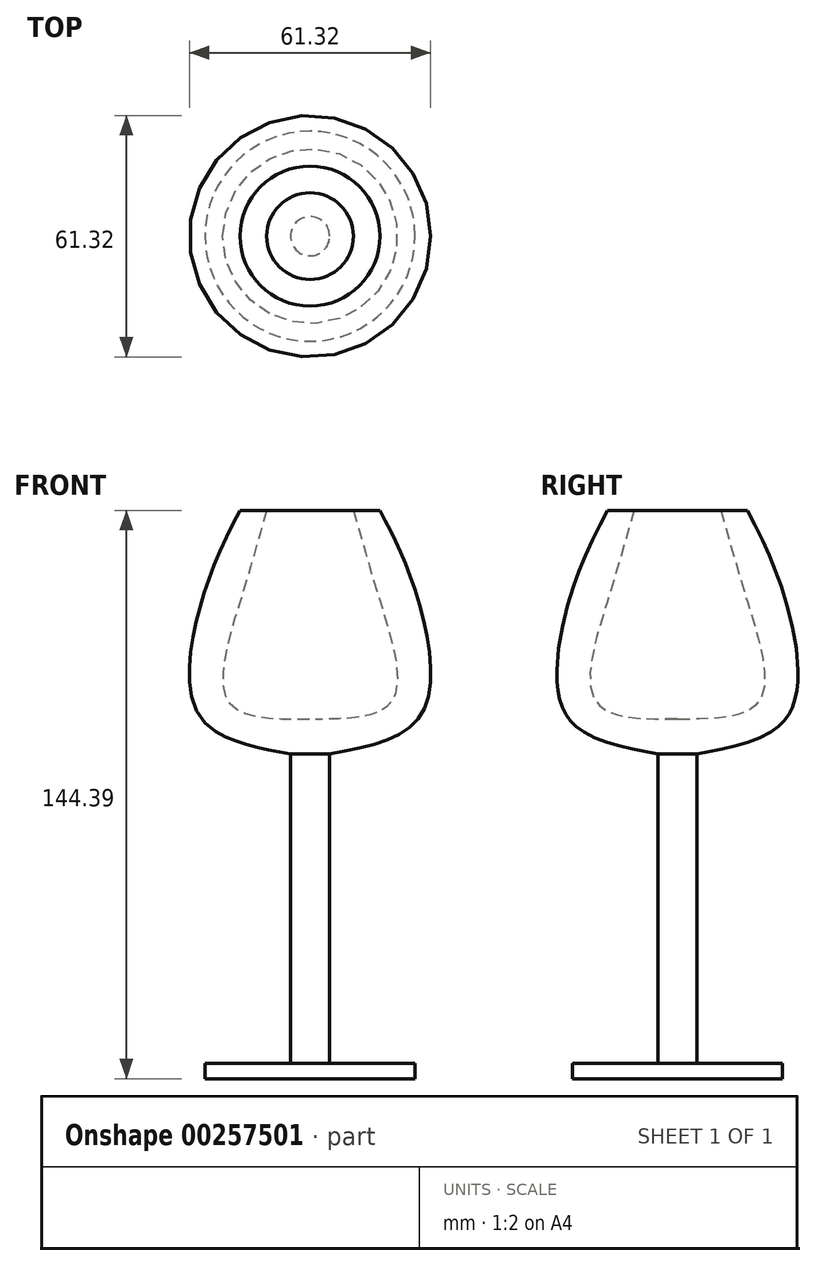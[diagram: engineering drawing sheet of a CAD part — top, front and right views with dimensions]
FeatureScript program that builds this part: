
annotation { "Feature Type Name" : "Feature", "Feature Type Description" : "" }
export const myFeature = defineFeature(function(context is Context, id is Id, definition is map)
    precondition{}
    {
        {
            var Q0;
            Q0=qCreatedBy(makeId("Front.planeOp"),FACE);
            var sketch = newSketch(context, id + "F0", { "sketchPlane" : qUnion([Q0])});
            skLineSegment(sketch, "E0", {"start": v(0, 84.82) * mm, "end": v(0, -87.3) * mm, "construction": true});
            skLineSegment(sketch, "E1", {"start": v(0, -75.57) * mm, "end": v(-26.67, -75.57) * mm});
            skLineSegment(sketch, "E2", {"start": v(-26.67, -75.57) * mm, "end": v(-26.67, -71.66) * mm});
            skLineSegment(sketch, "E3", {"start": v(-26.67, -71.66) * mm, "end": v(-4.98, -71.66) * mm});
            skLineSegment(sketch, "E4", {"start": v(-4.98, -71.66) * mm, "end": v(-4.98, 6.93) * mm});
            skFitSpline(sketch, "E5", {"points": [v(-4.98, 6.93) * mm, v(-28.45, 17.25) * mm, v(-26.67, 48.54) * mm, v(-17.78, 68.82) * mm], "startDerivative": vector(-89.02, 15.97) * mm, "endDerivative": vector(30.07, 57.85) * mm});
            skLineSegment(sketch, "E6", {"start": v(-17.78, 68.82) * mm, "end": v(-11.02, 68.82) * mm});
            skFitSpline(sketch, "E7", {"points": [v(-11.02, 68.82) * mm, v(-17.78, 45.7) * mm, v(-20.85, 20.45) * mm, v(0, 15.83) * mm], "startDerivative": vector(-17.88, -63.48) * mm, "endDerivative": vector(84.12, 0.65) * mm});
            skLineSegment(sketch, "E8", {"start": v(0, 15.83) * mm, "end": v(0, -75.57) * mm});
            skSolve(sketch);
        }
        {
            var Q0;
            Q0=makeQuery(id+"F0.imprint","IMPRINT",FACE,{"disambiguationData":[TD([[makeQuery(id+"F0.imprint","IMPRINT",EDGE,{"derivedFrom":sQuery(id+"F0.wireOp",EDGE,"E1")}),-1.0]])]});
            var Q1;
            Q1=sQuery(id+"F0.wireOp",EDGE,"E0");
            revolve(context, id + "F1", {"entities" : qUnion([Q0]), "axis" : qUnion([Q1]), "revolveType" : RevolveType.FULL});
        }
    });
